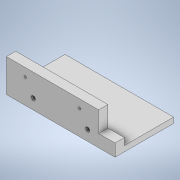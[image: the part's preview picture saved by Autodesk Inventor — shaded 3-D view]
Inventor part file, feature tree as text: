
AUTODESK INVENTOR PART (.ipt)
format: ipt  version: 2020 (Build 240168000, 168)  size: 192,512 bytes
history: native  units: mm
features: other x4, mirror x1
ambient origin geometry x8: Origin, YZ Plane, XZ Plane, XY Plane, X Axis, Y Axis, Z Axis, Center Point
bodies: Body1 (feature_tree)
feature tree (5):
  other  "side_bumper_lower_R.ipt"
  mirror  "미러1"
  other  "솔리드1::side_bumper_lower_R.ipt"
  other  "피쳐 태그1"
  other  "솔리드1"
